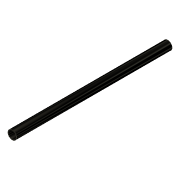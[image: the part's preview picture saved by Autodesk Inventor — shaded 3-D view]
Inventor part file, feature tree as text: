
AUTODESK INVENTOR PART (.ipt)
format: ipt  version: 2022 (Build 260153000, 153)  size: 82,432 bytes
history: native  units: mm
features: extrude x1, sketch x1
ambient origin geometry x8: Origin, YZ Plane, XZ Plane, XY Plane, X Axis, Y Axis, Z Axis, Center Point
bodies: Solid1 (feature_tree)
feature tree (2):
  extrude  "Extrusion1"  Depth=1000.0mm
  sketch  "Sketch1"  dims[d2=1000.0mm d3=0.0mm d4=50.8mm d5=57.15mm]
